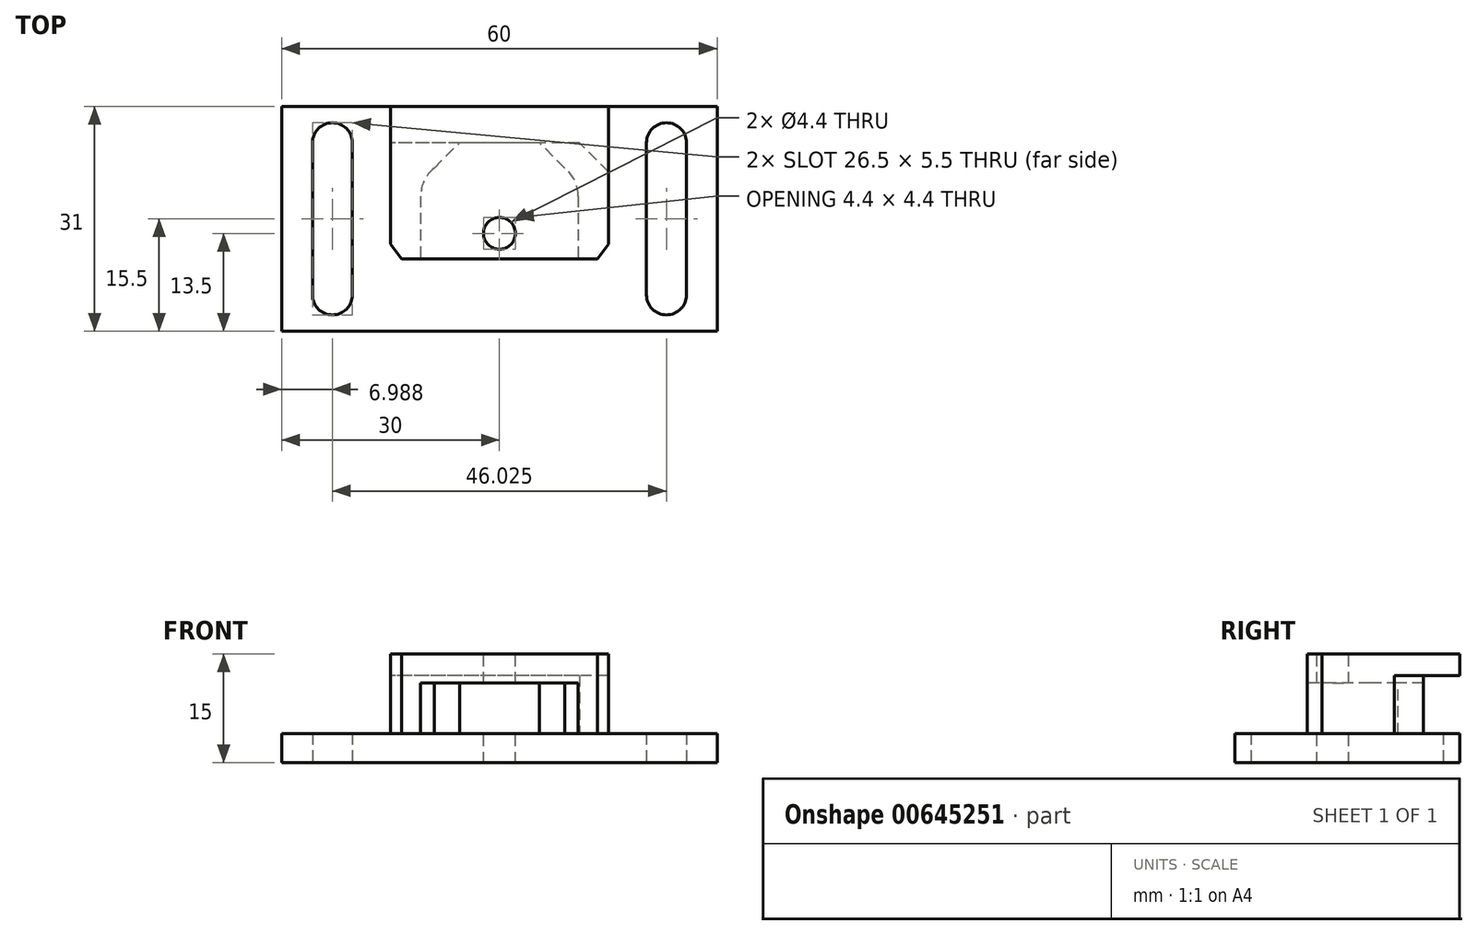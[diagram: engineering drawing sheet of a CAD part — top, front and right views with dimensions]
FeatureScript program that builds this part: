
annotation { "Feature Type Name" : "Feature", "Feature Type Description" : "" }
export const myFeature = defineFeature(function(context is Context, id is Id, definition is map)
    precondition{}
    {
        {
            var Q0;
            Q0=qCreatedBy(makeId("Top.planeOp"),FACE);
            var sketch = newSketch(context, id + "F0", { "sketchPlane" : qUnion([Q0])});
            skLineSegment(sketch, "E0.bottom", {"start": v(-15, 13) * mm, "end": v(15, 13) * mm});
            skLineSegment(sketch, "E0.top", {"start": v(-15, -13) * mm, "end": v(15, -13) * mm});
            skLineSegment(sketch, "E0.left", {"start": v(-15, 13) * mm, "end": v(-15, -13) * mm});
            skLineSegment(sketch, "E0.right", {"start": v(15, 13) * mm, "end": v(15, -13) * mm});
            skSolve(sketch);
        }
        {
            var Q0;
            Q0=qSketchRegion(id+"F0",true);
            extrude(context, id + "F1", {"entities" : qUnion([Q0]), "depth" : 15 * mm, "offsetDistance" : 25 * mm});
        }
        {
            var Q0;
            Q0=makeQuery(id+"F1.opExtrude","SWEPT_FACE",FACE,{"disambiguationData":[OSD([sQuery(id+"F0.wireOp",EDGE,"E0.top")])]});
            var sketch = newSketch(context, id + "F2", { "sketchPlane" : qUnion([Q0])});
            skLineSegment(sketch, "E1.bottom", {"start": v(-10.85, 11) * mm, "end": v(10.85, 11) * mm});
            skLineSegment(sketch, "E1.top", {"start": v(-10.85, 4) * mm, "end": v(10.85, 4) * mm});
            skLineSegment(sketch, "E1.left", {"start": v(-10.85, 11) * mm, "end": v(-10.85, 4) * mm});
            skLineSegment(sketch, "E1.right", {"start": v(10.85, 11) * mm, "end": v(10.85, 4) * mm});
            skSolve(sketch);
        }
        {
            var Q0;
            Q0=makeQuery(id+"F1.opExtrude","SWEPT_EDGE",EDGE,{"disambiguationData":[OSD([sQuery(id+"F0.wireOp",EDGE,"E0.top"),sQuery(id+"F0.wireOp",EDGE,"E0.left")])]});
            var Q1;
            Q1=makeQuery(id+"F1.opExtrude","SWEPT_EDGE",EDGE,{"disambiguationData":[OSD([sQuery(id+"F0.wireOp",EDGE,"E0.top"),sQuery(id+"F0.wireOp",EDGE,"E0.right")])]});
            chamfer(context, id + "F3", {"entities" : qUnion([Q0, Q1]), "chamferType" : ChamferType.TWO_OFFSETS, "width1" : 1.5 * mm, "oppositeDirection" : false, "width2" : 2 * mm, "tangentPropagation" : true});
        }
        {
            var Q0;
            Q0=makeQuery(id+"F1.opExtrude","SWEPT_FACE",FACE,{"disambiguationData":[OSD([sQuery(id+"F0.wireOp",EDGE,"E0.left")])]});
            var sketch = newSketch(context, id + "F4", { "sketchPlane" : qUnion([Q0])});
            skLineSegment(sketch, "E2", {"start": v(-13, 0) * mm, "end": v(-8, 0) * mm});
            skLineSegment(sketch, "E3", {"start": v(-8, 0) * mm, "end": v(-8, 4) * mm});
            skLineSegment(sketch, "E4", {"start": v(-8, 4) * mm, "end": v(-3, 4) * mm});
            skLineSegment(sketch, "E5", {"start": v(-3, 4) * mm, "end": v(-3, 12) * mm});
            skLineSegment(sketch, "E6", {"start": v(-3, 12) * mm, "end": v(-13, 12) * mm});
            skLineSegment(sketch, "E7", {"start": v(-13, 12) * mm, "end": v(-13, 0) * mm});
            skSolve(sketch);
        }
        {
            var Q0;
            Q0=qSketchRegion(id+"F4",true);
            extrude(context, id + "F5", {"entities" : qUnion([Q0]), "operationType" : NewBodyOperationType.REMOVE, "endBound" : BoundingType.THROUGH_ALL, "oppositeDirection" : true, "depth" : 25 * mm, "offsetDistance" : 25 * mm});
        }
        {
            var Q0;
            Q0=makeQuery(id+"F5.boolean.opBoolean","COPY",EDGE,{"derivedFrom":makeQuery(id+"F5.opExtrude","CAP_EDGE",EDGE,{"disambiguationData":[OSD([sQuery(id+"F4.wireOp",EDGE,"E5")])],"isStart":true})});
            var Q1;
            Q1=makeQuery(id+"F5.boolean.opBoolean","INTERSECT",EDGE,{"derivedFrom":[makeQuery(id+"F1.opExtrude","SWEPT_FACE",FACE,{"disambiguationData":[OSD([sQuery(id+"F0.wireOp",EDGE,"E0.right")])]}),makeQuery(id+"F5.opExtrude","SWEPT_FACE",FACE,{"disambiguationData":[OSD([sQuery(id+"F4.wireOp",EDGE,"E5")])]})]});
            chamfer(context, id + "F6", {"entities" : qUnion([Q0, Q1]), "width" : 4 * mm, "tangentPropagation" : true});
        }
        {
            var Q0;
            Q0=qSketchRegion(id+"F2",true);
            extrude(context, id + "F7", {"entities" : qUnion([Q0]), "operationType" : NewBodyOperationType.REMOVE, "oppositeDirection" : true, "depth" : 12.5 * mm, "offsetDistance" : 25 * mm});
        }
        {
            var Q0;
            Q0=makeQuery(id+"F5.boolean.opBoolean","COPY",FACE,{"derivedFrom":makeQuery(id+"F5.opExtrude","SWEPT_FACE",FACE,{"disambiguationData":[OSD([sQuery(id+"F4.wireOp",EDGE,"E5")])]})});
            var sketch = newSketch(context, id + "F8", { "sketchPlane" : qUnion([Q0])});
            skLineSegment(sketch, "E8.bottom", {"start": v(-5.5, 11) * mm, "end": v(5.5, 11) * mm});
            skLineSegment(sketch, "E8.top", {"start": v(-5.5, 4) * mm, "end": v(5.5, 4) * mm});
            skLineSegment(sketch, "E8.left", {"start": v(-5.5, 11) * mm, "end": v(-5.5, 4) * mm});
            skLineSegment(sketch, "E8.right", {"start": v(5.5, 11) * mm, "end": v(5.5, 4) * mm});
            skSolve(sketch);
        }
        {
            var Q0;
            Q0=qSketchRegion(id+"F8",true);
            extrude(context, id + "F9", {"entities" : qUnion([Q0]), "operationType" : NewBodyOperationType.REMOVE, "oppositeDirection" : true, "depth" : 4 * mm, "offsetDistance" : 25 * mm});
        }
        {
            var Q0;
            Q0=makeQuery(id+"F1.opExtrude","CAP_FACE",FACE,{"disambiguationData":[OSD([sQuery(id+"F0.wireOp",EDGE,"E0.bottom"),sQuery(id+"F0.wireOp",EDGE,"E0.top"),sQuery(id+"F0.wireOp",EDGE,"E0.left"),sQuery(id+"F0.wireOp",EDGE,"E0.right")])],"isStart":false});
            var sketch = newSketch(context, id + "F10", { "sketchPlane" : qUnion([Q0])});
            skLineSegment(sketch, "E9.bottom", {"start": v(15, 13) * mm, "end": v(-15, 13) * mm});
            skLineSegment(sketch, "E9.top", {"start": v(15, 8) * mm, "end": v(-15, 8) * mm});
            skLineSegment(sketch, "E9.left", {"start": v(15, 13) * mm, "end": v(15, 8) * mm});
            skLineSegment(sketch, "E9.right", {"start": v(-15, 13) * mm, "end": v(-15, 8) * mm});
            skSolve(sketch);
        }
        {
            var Q0;
            Q0=qSketchRegion(id+"F10",true);
            extrude(context, id + "F11", {"entities" : qUnion([Q0]), "operationType" : NewBodyOperationType.REMOVE, "endBound" : BoundingType.THROUGH_ALL, "oppositeDirection" : true, "depth" : 25 * mm, "offsetDistance" : 25 * mm});
        }
        {
            var Q0;
            Q0=makeQuery(id+"F1.opExtrude","CAP_FACE",FACE,{"disambiguationData":[OSD([sQuery(id+"F0.wireOp",EDGE,"E0.bottom"),sQuery(id+"F0.wireOp",EDGE,"E0.top"),sQuery(id+"F0.wireOp",EDGE,"E0.left"),sQuery(id+"F0.wireOp",EDGE,"E0.right")])],"isStart":false});
            var sketch = newSketch(context, id + "F12", { "sketchPlane" : qUnion([Q0])});
            skPoint(sketch, "E10", {"position": v(0, -9.5) * mm});
            skPoint(sketch, "E10.positionSnap0", {"position": v(0, -13) * mm});
            skSolve(sketch);
        }
        {
            var Q0;
            Q0=sQuery(id+"F12.wireOp",VERTEX,"E10");
            var Q1;
            Q1=makeQuery(id+"F1.opExtrude","SWEPT_BODY",BODY,{"disambiguationData":[OSD([sQuery(id+"F0.wireOp",EDGE,"E0.bottom"),sQuery(id+"F0.wireOp",EDGE,"E0.top"),sQuery(id+"F0.wireOp",EDGE,"E0.left"),sQuery(id+"F0.wireOp",EDGE,"E0.right")])]});
            hole(context, id + "F13", {"style" : HoleStyle.SIMPLE, "endStyle" : HoleEndStyle.THROUGH, "standardTappedOrClearance" : lookupTablePath({ "standard" : "ISO", "fit" : "Normal", "size" : "M4", "type" : "Clearance" }), "standardBlindInLast" : lookupTablePath({ "fit" : "Standard", "standard" : "ISO", "size" : "M4", "type" : "Clearance" }), "holeDiameter" : 4.4 * mm, "majorDiameter" : 5 * mm, "isTappedThrough" : true, "tappedDepth" : 12 * mm, "tapClearance" : 3, "locations" : qUnion([Q0]), "scope" : qUnion([Q1])});
        }
        {
            var Q0;
            Q0=makeQuery(id+"F1.opExtrude","CAP_FACE",FACE,{"disambiguationData":[OSD([sQuery(id+"F0.wireOp",EDGE,"E0.bottom"),sQuery(id+"F0.wireOp",EDGE,"E0.top"),sQuery(id+"F0.wireOp",EDGE,"E0.left"),sQuery(id+"F0.wireOp",EDGE,"E0.right")])],"isStart":true});
            var sketch = newSketch(context, id + "F14", { "sketchPlane" : qUnion([Q0])});
            skLineSegment(sketch, "E11.top", {"start": v(-30, 23) * mm, "end": v(30, 23) * mm});
            skLineSegment(sketch, "E11.left", {"start": v(-30, 11) * mm, "end": v(-30, 23) * mm});
            skLineSegment(sketch, "E11.right", {"start": v(30, 11) * mm, "end": v(30, 23) * mm});
            skLineSegment(sketch, "E12.bottom", {"start": v(15, 11) * mm, "end": v(30, 11) * mm});
            skLineSegment(sketch, "E12.top", {"start": v(15, -8) * mm, "end": v(30, -8) * mm});
            skLineSegment(sketch, "E12.left", {"start": v(15, 11) * mm, "end": v(15, -8) * mm});
            skLineSegment(sketch, "E12.right", {"start": v(30, 11) * mm, "end": v(30, -8) * mm});
            skLineSegment(sketch, "E13.MirrorCS", {"start": v(-15, 11) * mm, "end": v(-30, 11) * mm});
            skLineSegment(sketch, "E14.MirrorCS", {"start": v(-30, 11) * mm, "end": v(-30, -8) * mm});
            skLineSegment(sketch, "E15.MirrorCS", {"start": v(-15, -8) * mm, "end": v(-30, -8) * mm});
            skLineSegment(sketch, "E16.MirrorCS", {"start": v(-15, 11) * mm, "end": v(-15, -8) * mm});
            skPoint(sketch, "E17.orphan", {"position": v(-30, 13) * mm});
            skPoint(sketch, "E18.orphan", {"position": v(30, 13) * mm});
            skLineSegment(sketch, "E19", {"start": v(15, 11) * mm, "end": v(13.5, 13) * mm});
            skLineSegment(sketch, "E20", {"start": v(13.5, 13) * mm, "end": v(-13.5, 13) * mm});
            skLineSegment(sketch, "E21", {"start": v(-13.5, 13) * mm, "end": v(-15, 11) * mm});
            skLineSegment(sketch, "E22.left", {"start": v(25.76, -3) * mm, "end": v(25.76, 18) * mm});
            skLineSegment(sketch, "E22.right", {"start": v(20.26, -3) * mm, "end": v(20.26, 18) * mm});
            skArc(sketch, "E23", {"start": v(20.26, -3) * mm, "mid": v(23.01, -5.75) * mm, "end": v(25.76, -3) * mm});
            skArc(sketch, "E24", {"start": v(25.76, 18) * mm, "mid": v(23.01, 20.75) * mm, "end": v(20.26, 18) * mm});
            skArc(sketch, "E25.MirrorCS", {"start": v(-20.26, -3) * mm, "mid": v(-23.01, -5.75) * mm, "end": v(-25.76, -3) * mm});
            skLineSegment(sketch, "E26.MirrorCS", {"start": v(-20.26, -3) * mm, "end": v(-20.26, 18) * mm});
            skArc(sketch, "E27.MirrorCS", {"start": v(-25.76, 18) * mm, "mid": v(-23.01, 20.75) * mm, "end": v(-20.26, 18) * mm});
            skLineSegment(sketch, "E28.MirrorCS", {"start": v(-25.76, -3) * mm, "end": v(-25.76, 18) * mm});
            skSolve(sketch);
        }
        {
            var Q0;
            Q0=qSketchRegion(id+"F14",true);
            extrude(context, id + "F15", {"entities" : qUnion([Q0]), "operationType" : NewBodyOperationType.ADD, "oppositeDirection" : true, "depth" : 4 * mm, "offsetDistance" : 25 * mm});
        }
        {
            var Q0;
            Q0=makeQuery(id+"F9.boolean.opBoolean","INTERSECT",EDGE,{"derivedFrom":[makeQuery(id+"F7.boolean.opBoolean","COPY",FACE,{"derivedFrom":makeQuery(id+"F7.opExtrude","CAP_FACE",FACE,{"disambiguationData":[OSD([sQuery(id+"F2.wireOp",EDGE,"E1.bottom"),sQuery(id+"F2.wireOp",EDGE,"E1.top"),sQuery(id+"F2.wireOp",EDGE,"E1.left"),sQuery(id+"F2.wireOp",EDGE,"E1.right")])],"isStart":false})}),makeQuery(id+"F9.opExtrude","SWEPT_FACE",FACE,{"disambiguationData":[OSD([sQuery(id+"F8.wireOp",EDGE,"E8.right")])]})]});
            chamfer(context, id + "F16", {"entities" : qUnion([Q0]), "width" : 3.5 * mm, "tangentPropagation" : true});
        }
        {
            var Q0;
            Q0=makeQuery(id+"F7.boolean.opBoolean","COPY",EDGE,{"derivedFrom":makeQuery(id+"F7.opExtrude","CAP_EDGE",EDGE,{"disambiguationData":[OSD([sQuery(id+"F2.wireOp",EDGE,"E1.left")])],"isStart":false})});
            fillet(context, id + "F17", {"entities" : qUnion([Q0]), "radius" : 5 * mm, "tangentPropagation" : true, "allowEdgeOverflow" : false});
        }
        {
            var Q0;
            Q0=makeQuery(id+"F9.boolean.opBoolean","INTERSECT",EDGE,{"derivedFrom":[makeQuery(id+"F7.boolean.opBoolean","COPY",FACE,{"derivedFrom":makeQuery(id+"F7.opExtrude","CAP_FACE",FACE,{"disambiguationData":[OSD([sQuery(id+"F2.wireOp",EDGE,"E1.bottom"),sQuery(id+"F2.wireOp",EDGE,"E1.top"),sQuery(id+"F2.wireOp",EDGE,"E1.left"),sQuery(id+"F2.wireOp",EDGE,"E1.right")])],"isStart":false})}),makeQuery(id+"F9.opExtrude","SWEPT_FACE",FACE,{"disambiguationData":[OSD([sQuery(id+"F8.wireOp",EDGE,"E8.left")])]})]});
            chamfer(context, id + "F18", {"entities" : qUnion([Q0]), "width" : 3.5 * mm, "tangentPropagation" : true});
        }
        {
            var Q0;
            Q0=makeQuery(id+"F7.boolean.opBoolean","COPY",EDGE,{"derivedFrom":makeQuery(id+"F7.opExtrude","CAP_EDGE",EDGE,{"disambiguationData":[OSD([sQuery(id+"F2.wireOp",EDGE,"E1.right")])],"isStart":false})});
            fillet(context, id + "F19", {"entities" : qUnion([Q0]), "radius" : 5 * mm, "tangentPropagation" : true, "allowEdgeOverflow" : false});
        }
    });
